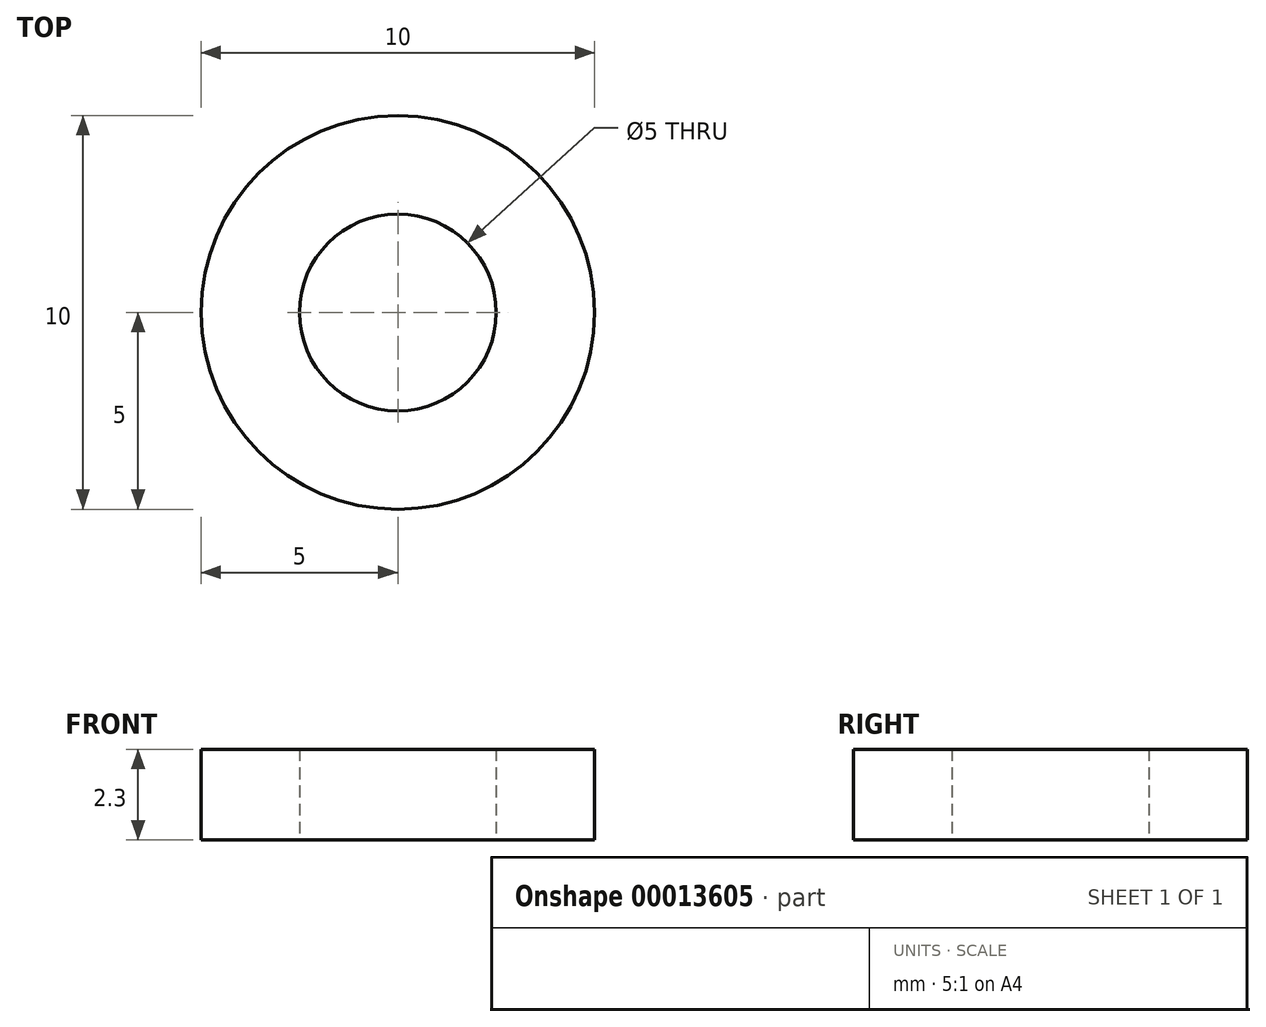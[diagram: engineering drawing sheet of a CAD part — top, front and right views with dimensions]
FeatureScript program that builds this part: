
annotation { "Feature Type Name" : "Feature", "Feature Type Description" : "" }
export const myFeature = defineFeature(function(context is Context, id is Id, definition is map)
    precondition{}
    {
        {
            var Q0;
            Q0=qCreatedBy(makeId("Top.planeOp"),FACE);
            var sketch = newSketch(context, id + "F0", { "sketchPlane" : qUnion([Q0])});
            skCircle(sketch, "E0", {"center": v(0, 0) * mm, "radius": 2.5 * mm});
            skCircle(sketch, "E1", {"center": v(0, 0) * mm, "radius": 5 * mm});
            skSolve(sketch);
        }
        {
            var Q0;
            Q0=makeQuery(id+"F0.imprint","IMPRINT",FACE,{"disambiguationData":[TD([[makeQuery(id+"F0.imprint","IMPRINT",EDGE,{"derivedFrom":sQuery(id+"F0.wireOp",EDGE,"E0")}),-1.0]])]});
            extrude(context, id + "F1", {"entities" : qUnion([Q0]), "depth" : 2.3 * mm});
        }
    });
